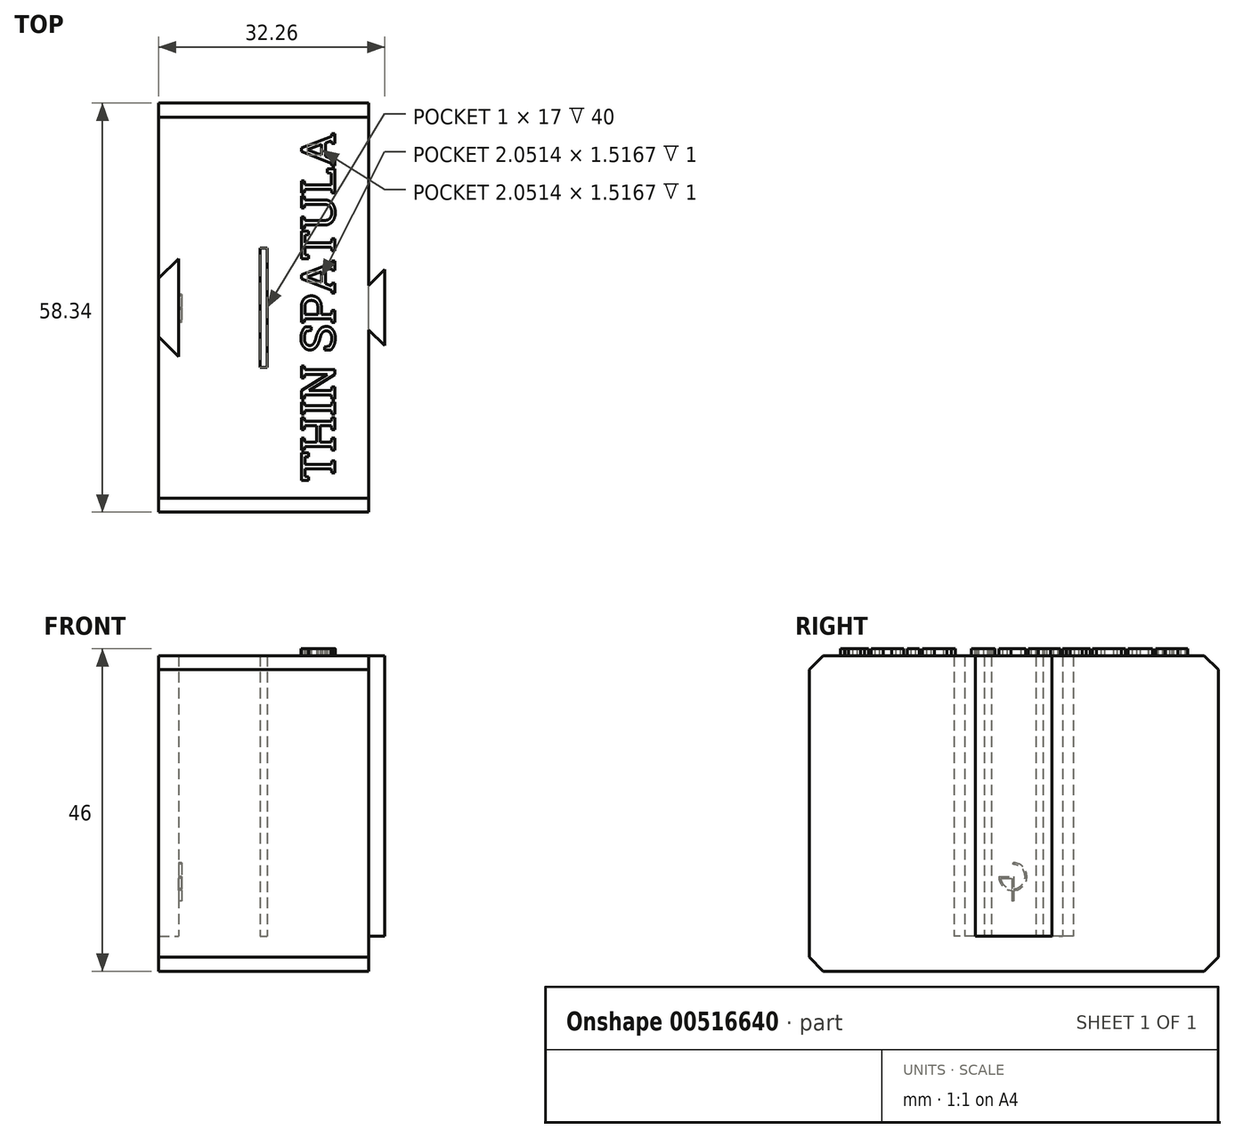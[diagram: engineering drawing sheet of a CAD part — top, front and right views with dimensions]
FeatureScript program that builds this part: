
annotation { "Feature Type Name" : "Feature", "Feature Type Description" : "" }
export const myFeature = defineFeature(function(context is Context, id is Id, definition is map)
    precondition{}
    {
        {
            var Q0;
            Q0=qCreatedBy(makeId("Top.planeOp"),FACE);
            var sketch = newSketch(context, id + "F0", { "sketchPlane" : qUnion([Q0])});
            skLineSegment(sketch, "E0", {"start": v(-15, 4.17) * mm, "end": v(-15, 29.17) * mm});
            skLineSegment(sketch, "E1", {"start": v(-15, 29.17) * mm, "end": v(15, 29.17) * mm});
            skLineSegment(sketch, "E2", {"start": v(15, 29.17) * mm, "end": v(15, 3.17) * mm});
            skLineSegment(sketch, "E3", {"start": v(-15, 4.17) * mm, "end": v(-12.17, 7) * mm});
            skLineSegment(sketch, "E4", {"start": v(-12.17, 7) * mm, "end": v(-12.17, 0) * mm});
            skLineSegment(sketch, "E5", {"start": v(15, 3.17) * mm, "end": v(17.26, 5.43) * mm});
            skLineSegment(sketch, "E6", {"start": v(17.26, 5.43) * mm, "end": v(17.26, -0.57) * mm});
            skLineSegment(sketch, "E7.MirrorCS", {"start": v(-15, -4.17) * mm, "end": v(-12.17, -7) * mm});
            skLineSegment(sketch, "E8.MirrorCS", {"start": v(15, -29.17) * mm, "end": v(15, -3.17) * mm});
            skLineSegment(sketch, "E9.MirrorCS", {"start": v(-12.17, -7) * mm, "end": v(-12.17, 0) * mm});
            skLineSegment(sketch, "E10.MirrorCS", {"start": v(-15, -4.17) * mm, "end": v(-15, -29.17) * mm});
            skLineSegment(sketch, "E11.MirrorCS", {"start": v(17.26, -5.43) * mm, "end": v(17.26, 0.57) * mm});
            skLineSegment(sketch, "E12.MirrorCS", {"start": v(15, -3.17) * mm, "end": v(17.26, -5.43) * mm});
            skLineSegment(sketch, "E13.MirrorCS", {"start": v(-15, -29.17) * mm, "end": v(15, -29.17) * mm});
            skLineSegment(sketch, "E14.bottom", {"start": v(-0.5, 8.5) * mm, "end": v(0.5, 8.5) * mm});
            skLineSegment(sketch, "E14.top", {"start": v(-0.5, -8.5) * mm, "end": v(0.5, -8.5) * mm});
            skLineSegment(sketch, "E14.left", {"start": v(-0.5, 8.5) * mm, "end": v(-0.5, -8.5) * mm});
            skLineSegment(sketch, "E14.right", {"start": v(0.5, 8.5) * mm, "end": v(0.5, -8.5) * mm});
            skPoint(sketch, "E14.middle", {"position": v(0, 0) * mm});
            skLineSegment(sketch, "E15", {"start": v(15, 3.17) * mm, "end": v(15, -3.17) * mm});
            skLineSegment(sketch, "E16", {"start": v(-15, -4.17) * mm, "end": v(-15, 4.17) * mm});
            skSolve(sketch);
        }
        {
            var Q0;
            Q0=makeQuery(id+"F0.imprint","IMPRINT",FACE,{"disambiguationData":[TD([[makeQuery(id+"F0.imprint","IMPRINT",EDGE,{"derivedFrom":sQuery(id+"F0.wireOp",EDGE,"E0")}),-1.0]])]});
            var Q1;
            Q1=makeQuery(id+"F0.imprint","IMPRINT",FACE,{"disambiguationData":[TD([[makeQuery(id+"F0.imprint","IMPRINT",EDGE,{"derivedFrom":sQuery(id+"F0.wireOp",EDGE,"E5")}),-1.0]])]});
            extrude(context, id + "F1", {"entities" : qUnion([Q0, Q1]), "depth" : 40 * mm, "offsetDistance" : 25 * mm});
        }
        {
            var Q0;
            Q0=makeQuery(id+"F0.imprint","IMPRINT",FACE,{"disambiguationData":[TD([[makeQuery(id+"F0.imprint","IMPRINT",EDGE,{"derivedFrom":sQuery(id+"F0.wireOp",EDGE,"E0")}),-1.0]])]});
            var Q1;
            Q1=makeQuery(id+"F0.imprint","IMPRINT",FACE,{"disambiguationData":[TD([[makeQuery(id+"F0.imprint","IMPRINT",EDGE,{"derivedFrom":sQuery(id+"F0.wireOp",EDGE,"E14.bottom")}),-1.0]])]});
            var Q2;
            Q2=makeQuery(id+"F0.imprint","IMPRINT",FACE,{"disambiguationData":[TD([[makeQuery(id+"F0.imprint","IMPRINT",EDGE,{"derivedFrom":sQuery(id+"F0.wireOp",EDGE,"E3")}),-1.0]])]});
            extrude(context, id + "F2", {"entities" : qUnion([Q0, Q1, Q2]), "operationType" : NewBodyOperationType.ADD, "oppositeDirection" : true, "depth" : 5 * mm, "offsetDistance" : 25 * mm});
        }
        {
            var Q0;
            Q0=makeQuery(id+"F2.opExtrude","CAP_EDGE",EDGE,{"disambiguationData":[OSD([sQuery(id+"F0.wireOp",EDGE,"E13.MirrorCS")])],"isStart":false});
            var Q1;
            Q1=makeQuery(id+"F2.opExtrude","CAP_EDGE",EDGE,{"disambiguationData":[OSD([sQuery(id+"F0.wireOp",EDGE,"E1")])],"isStart":false});
            var Q2;
            Q2=makeQuery(id+"F1.opExtrude","CAP_EDGE",EDGE,{"disambiguationData":[OSD([sQuery(id+"F0.wireOp",EDGE,"E13.MirrorCS")])],"isStart":false});
            var Q3;
            Q3=makeQuery(id+"F1.opExtrude","CAP_EDGE",EDGE,{"disambiguationData":[OSD([sQuery(id+"F0.wireOp",EDGE,"E1")])],"isStart":false});
            chamfer(context, id + "F3", {"entities" : qUnion([Q0, Q1, Q2, Q3]), "width" : 2 * mm, "tangentPropagation" : true});
        }
        {
            var Q0;
            Q0=makeQuery(id+"F1.opExtrude","CAP_FACE",FACE,{"disambiguationData":[OSD([sQuery(id+"F0.wireOp",EDGE,"E0"),sQuery(id+"F0.wireOp",EDGE,"E1"),sQuery(id+"F0.wireOp",EDGE,"E2"),sQuery(id+"F0.wireOp",EDGE,"E3"),sQuery(id+"F0.wireOp",EDGE,"E4"),sQuery(id+"F0.wireOp",EDGE,"E5"),sQuery(id+"F0.wireOp",EDGE,"E6"),sQuery(id+"F0.wireOp",EDGE,"E7.MirrorCS"),sQuery(id+"F0.wireOp",EDGE,"E8.MirrorCS"),sQuery(id+"F0.wireOp",EDGE,"E9.MirrorCS"),sQuery(id+"F0.wireOp",EDGE,"E10.MirrorCS"),sQuery(id+"F0.wireOp",EDGE,"E11.MirrorCS"),sQuery(id+"F0.wireOp",EDGE,"E12.MirrorCS"),sQuery(id+"F0.wireOp",EDGE,"E13.MirrorCS"),sQuery(id+"F0.wireOp",EDGE,"E14.bottom"),sQuery(id+"F0.wireOp",EDGE,"E14.top"),sQuery(id+"F0.wireOp",EDGE,"E14.left"),sQuery(id+"F0.wireOp",EDGE,"E14.right")])],"isStart":false});
            var sketch = newSketch(context, id + "F4", { "sketchPlane" : qUnion([Q0])});
            skText(sketch, "E17", { "text": "THIN SPATULA", "fontName": "RobotoSlab-Regular.ttf"});
            const initialGuessF4  = {"E17": [0.01014, -0.0248, 0, 1, 0.00484]};
            skSetInitialGuess(sketch, initialGuessF4);
            skSolve(sketch);
        }
        {
            var Q0;
            Q0=qSketchRegion(id+"F4",true);
            extrude(context, id + "F5", {"entities" : qUnion([Q0]), "operationType" : NewBodyOperationType.ADD, "depth" : 1 * mm});
        }
        {
            var Q0;
            Q0=makeQuery(id+"F1.opExtrude","SWEPT_FACE",FACE,{"disambiguationData":[OSD([sQuery(id+"F0.wireOp",EDGE,"E4"),sQuery(id+"F0.wireOp",EDGE,"E9.MirrorCS")])]});
            var sketch = newSketch(context, id + "F6", { "sketchPlane" : qUnion([Q0])});
            skLineSegment(sketch, "E18.bottom", {"start": v(0.12, 10.5) * mm, "end": v(2.12, 10.5) * mm, "construction": true});
            skLineSegment(sketch, "E18.top", {"start": v(0.12, 8.5) * mm, "end": v(2.12, 8.5) * mm, "construction": true});
            skLineSegment(sketch, "E18.left", {"start": v(0.12, 10.5) * mm, "end": v(0.12, 8.5) * mm, "construction": true});
            skLineSegment(sketch, "E18.right", {"start": v(2.12, 10.5) * mm, "end": v(2.12, 8.5) * mm, "construction": true});
            skArc(sketch, "E19", {"start": v(0.12, 10.5) * mm, "mid": v(-1.3, 7.09) * mm, "end": v(2.12, 8.5) * mm});
            skLineSegment(sketch, "E20", {"start": v(0.12, 10.5) * mm, "end": v(0.12, 10.25) * mm});
            skLineSegment(sketch, "E21", {"start": v(2.12, 8.5) * mm, "end": v(1.87, 8.5) * mm});
            skArc(sketch, "E22", {"start": v(0.12, 10.25) * mm, "mid": v(-1.12, 7.26) * mm, "end": v(1.87, 8.5) * mm});
            skLineSegment(sketch, "E23", {"start": v(1.87, 8.5) * mm, "end": v(0, 8.5) * mm});
            skLineSegment(sketch, "E24", {"start": v(0, 8.5) * mm, "end": v(0, 5) * mm});
            skLineSegment(sketch, "E25", {"start": v(0, 5) * mm, "end": v(0.25, 5) * mm});
            skLineSegment(sketch, "E26", {"start": v(1.85, 8.25) * mm, "end": v(0.25, 8.25) * mm});
            skLineSegment(sketch, "E27", {"start": v(0.25, 8.25) * mm, "end": v(0.25, 5) * mm});
            skSolve(sketch);
        }
        {
            var Q0;
            {var subQ0=sQuery(id+"F6.wireOp",EDGE,"E20");Q0=makeQuery(id+"F6.imprint","IMPRINT",FACE,{"disambiguationData":[TD([[makeQuery(id+"F6.imprint","IMPRINT",EDGE,{"derivedFrom":subQ0}),-1.0]])]});}
            var Q1;
            {var subQ1=sQuery(id+"F6.wireOp",EDGE,"E23");Q1=makeQuery(id+"F6.imprint","IMPRINT",FACE,{"disambiguationData":[TD([[makeQuery(id+"F6.imprint","IMPRINT",EDGE,{"derivedFrom":subQ1}),1.0]])]});}
            var Q2;
            {var subQ1=sQuery(id+"F6.wireOp",EDGE,"E21");Q2=makeQuery(id+"F6.imprint","IMPRINT",FACE,{"disambiguationData":[TD([[makeQuery(id+"F6.imprint","IMPRINT",EDGE,{"derivedFrom":subQ1}),1.0]])]});}
            var Q3;
            {var subQ0=sQuery(id+"F6.wireOp",EDGE,"E24");var subQ1=sQuery(id+"F6.wireOp",EDGE,"E19");var subQ2=makeQuery(id+"F6.imprint","INTERSECT",VERTEX,{"derivedFrom":[subQ1,subQ0]});Q3=makeQuery(id+"F6.imprint","IMPRINT",FACE,{"disambiguationData":[TD([[makeQuery(id+"F6.imprint","IMPRINT",EDGE,{"disambiguationData":[TD([[subQ2,-1.0]])],"derivedFrom":subQ1}),1.0]])]});}
            var Q4;
            {var subQ5=sQuery(id+"F6.wireOp",EDGE,"E25");Q4=makeQuery(id+"F6.imprint","IMPRINT",FACE,{"disambiguationData":[TD([[makeQuery(id+"F6.imprint","IMPRINT",EDGE,{"derivedFrom":subQ5}),1.0]])]});}
            extrude(context, id + "F7", {"entities" : qUnion([Q0, Q1, Q2, Q3, Q4]), "operationType" : NewBodyOperationType.REMOVE, "oppositeDirection" : true, "depth" : .5 * mm, "offsetDistance" : 25 * mm});
        }
    });
